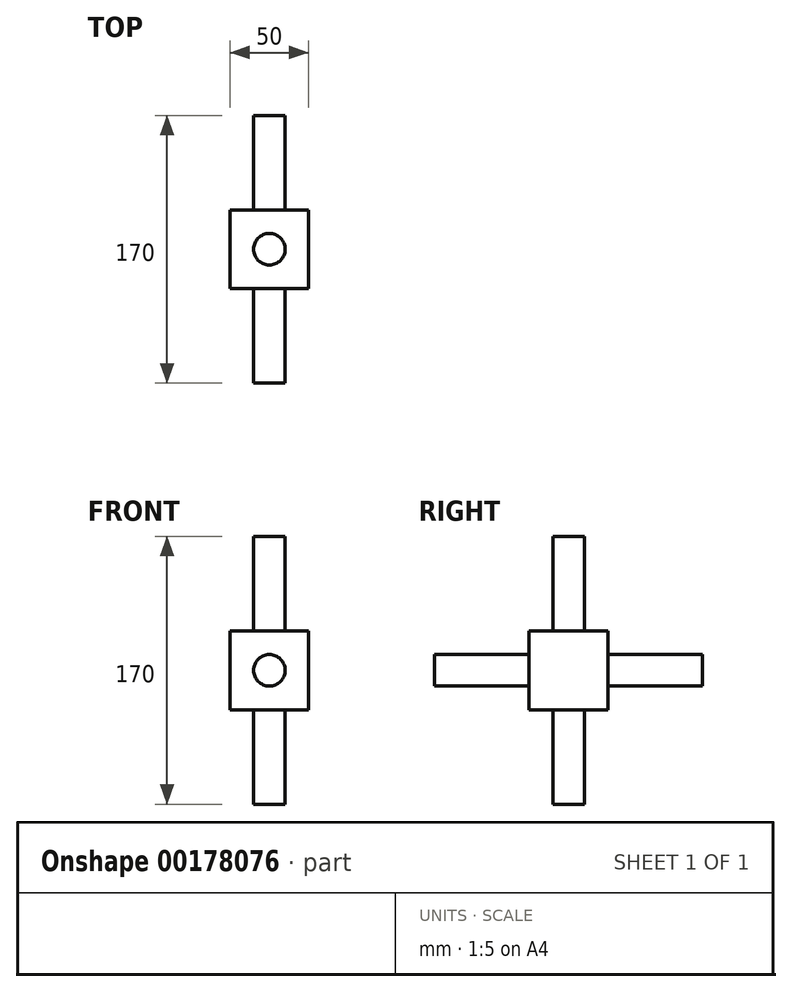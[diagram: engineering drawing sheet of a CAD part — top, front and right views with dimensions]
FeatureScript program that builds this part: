
annotation { "Feature Type Name" : "Feature", "Feature Type Description" : "" }
export const myFeature = defineFeature(function(context is Context, id is Id, definition is map)
    precondition{}
    {
        {
            var Q0;
            Q0=qCreatedBy(makeId("Top.planeOp"),FACE);
            var sketch = newSketch(context, id + "F0", { "sketchPlane" : qUnion([Q0])});
            skLineSegment(sketch, "E0.bottom", {"start": v(-25, 25) * mm, "end": v(25, 25) * mm});
            skLineSegment(sketch, "E0.top", {"start": v(-25, -25) * mm, "end": v(25, -25) * mm});
            skLineSegment(sketch, "E0.left", {"start": v(-25, 25) * mm, "end": v(-25, -25) * mm});
            skLineSegment(sketch, "E0.right", {"start": v(25, 25) * mm, "end": v(25, -25) * mm});
            skPoint(sketch, "E0.middle", {"position": v(0, 0) * mm});
            skSolve(sketch);
        }
        {
            var Q0;
            Q0 = qSketchRegion(id + "F0", true);
            extrude(context, id + "F1", {"entities" : qUnion([Q0]), "depth" : 25 * mm, "hasSecondDirection" : true, "secondDirectionOppositeDirection" : true, "secondDirectionDepth" : 25 * mm});
        }
        {
            var Q0;
            Q0=makeQuery(id+"F1.opExtrude","SWEPT_FACE",FACE,{"disambiguationData":[OSD([sQuery(id+"F0.wireOp",EDGE,"E0.top")])]});
            var sketch = newSketch(context, id + "F2", { "sketchPlane" : qUnion([Q0])});
            skCircle(sketch, "E1", {"center": v(0, 0) * mm, "radius": 10 * mm});
            skSolve(sketch);
        }
        {
            var Q0;
            Q0 = qSketchRegion(id + "F2", true);
            extrude(context, id + "F3", {"entities" : qUnion([Q0]), "operationType" : NewBodyOperationType.ADD, "depth" : 60 * mm});
        }
        {
            var Q0;
            Q0=makeQuery(id+"F1.opExtrude","CAP_FACE",FACE,{"disambiguationData":[OSD([sQuery(id+"F0.wireOp",EDGE,"E0.bottom"),sQuery(id+"F0.wireOp",EDGE,"E0.top"),sQuery(id+"F0.wireOp",EDGE,"E0.left"),sQuery(id+"F0.wireOp",EDGE,"E0.right")])],"isStart":false});
            var sketch = newSketch(context, id + "F4", { "sketchPlane" : qUnion([Q0])});
            skCircle(sketch, "E2", {"center": v(0, 0) * mm, "radius": 10 * mm});
            skSolve(sketch);
        }
        {
            var Q0;
            Q0 = qSketchRegion(id + "F4", true);
            extrude(context, id + "F5", {"entities" : qUnion([Q0]), "operationType" : NewBodyOperationType.ADD, "depth" : 60 * mm});
        }
        {
            var Q0;
            Q0=makeQuery(id+"F1.opExtrude","SWEPT_FACE",FACE,{"disambiguationData":[OSD([sQuery(id+"F0.wireOp",EDGE,"E0.bottom")])]});
            var sketch = newSketch(context, id + "F6", { "sketchPlane" : qUnion([Q0])});
            skCircle(sketch, "E3", {"center": v(0, 0) * mm, "radius": 10 * mm});
            skSolve(sketch);
        }
        {
            var Q0;
            Q0 = qSketchRegion(id + "F6", true);
            extrude(context, id + "F7", {"entities" : qUnion([Q0]), "operationType" : NewBodyOperationType.ADD, "depth" : 60 * mm});
        }
        {
            var Q0;
            Q0=makeQuery(id+"F1.opExtrude","CAP_FACE",FACE,{"disambiguationData":[OSD([sQuery(id+"F0.wireOp",EDGE,"E0.bottom"),sQuery(id+"F0.wireOp",EDGE,"E0.top"),sQuery(id+"F0.wireOp",EDGE,"E0.left"),sQuery(id+"F0.wireOp",EDGE,"E0.right")])],"isStart":true});
            var sketch = newSketch(context, id + "F8", { "sketchPlane" : qUnion([Q0])});
            skCircle(sketch, "E4", {"center": v(0, 0) * mm, "radius": 10 * mm});
            skSolve(sketch);
        }
        {
            var Q0;
            Q0 = qSketchRegion(id + "F8", true);
            extrude(context, id + "F9", {"entities" : qUnion([Q0]), "operationType" : NewBodyOperationType.ADD, "depth" : 60 * mm});
        }
    });
